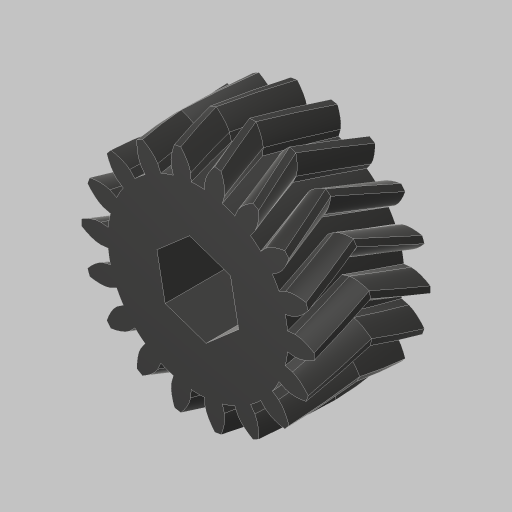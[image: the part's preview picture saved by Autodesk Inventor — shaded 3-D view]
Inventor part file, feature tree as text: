
AUTODESK INVENTOR PART (.ipt)
format: ipt  version: 2023.5 (Build 275446000, 446)  size: 654,336 bytes
history: native  units: in
note: dims shown in document units (in); Inventor stores cm internally (conversion verified against a paired STEP export)
features: other x2, extrude x1, sketch x1
ambient origin geometry x8: Origin, YZ Plane, XZ Plane, XY Plane, X Axis, Y Axis, Z Axis, Center Point
bodies: Solid1 (feature_tree)
feature tree (4):
  extrude  "Extrusion1"  TaperAngle=0.0deg  [1 undecoded]
  other  "DIAMETRIC PITCH"
  sketch  "Sketch1"  dims[d0=0.507in d1=0.0in d2=0.0in d3=1.4173in]
  other  "Helical 2M 18T"
note: 1 required parameter value undecoded (feature->parameter linkage not recoverable at this tier; creation-order binding heuristic only, values carry confidence <= 0.55)
